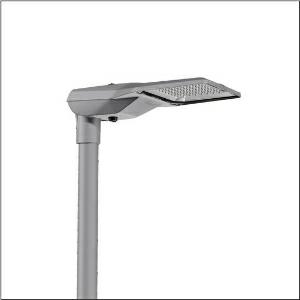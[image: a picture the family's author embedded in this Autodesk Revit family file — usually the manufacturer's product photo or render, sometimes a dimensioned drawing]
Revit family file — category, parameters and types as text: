
# Revit family: streetlight_sl_21_midi___st1_5a_5xe3p33t08lb_3dd1
name_source: partatom
category: Lighting Fixtures
units: mm (PartAtom-declared; Revit-internal decimal feet)

## family parameters
Cut with Voids When Loaded = No
Host = Face
Light Source = No
Part Type = Normal
Room Calculation Point = No
Round Connector Dimension = Use Diameter
Shared = No

## types (1)
- --- (1 x LED, 14100 lm, 99.6 W, 3000K)
    Apparent Load = 100 VA
    CIE Flux Codes = 22 53 95 100 100
    Color Rendering = 70
    Color Temperature = 3000K
    Default Elevation = 1800 mm
    Description = Streetlight SL 21 midi, mast luminaire, primary light control with lens, of PMMA, primary optical cover: cover, of toughened safety glass, transparent, light distribution: ST1.5a, light emission: direct distribution, primary light characteristic: asymmetric, installation type: side-entry, post-top, LED, High Power LED, rated luminous flux: 14.100lm, luminous efficacy: 142lm/W, light colour: 730, colour temperature: 3000K, control gear: D4i, control: overheat protection, constant luminous flux control, time-dependent luminous flux control, flexible luminous flux parameterisation, pre-setting: logarithmic dimming characteristic, mains connection: 230..240V, AC, 50/60Hz, start of lifetime: 100W, end of service life: 102W, reduction: 46W, luminaire housing, of diecast aluminium, powder-coated, SITECO metallic grey (DB 702S), corrosivity category C5 high according to DIN EN ISO 12944, please order mast flange separately, inclination adjustable: 0°, 5°, 10°, 15°, sealing non-destructively replaceable, multi-level sealing system, length: 644mm, width: 335mm, height: 110mm, mast flange for spigot size: 42mm (side-entry): 5XC10008XM4, 60/48mm (side-entry/post-top): 5XC10108XM2, 76/60mm (side-entry/post-top): 5XC10108XM1, mounting height: 4..8m, Smart Interface below and above, protection rating (complete): IP66, insulation class (complete): insulation class II (safety insulation), certification: CE, ENEC, ENEC+, VDE, impact resistance: IK10, permissible operating ambient temperature for outdoor applications: -40..+50°C, standard-compliant lighting for roads and squares, packaging unit: 1 piece

Light Distribution: ST1.5a
    Height = 111 mm
    Lamp = 1 x LED
    Lamp Light Flux = 14100 lm
    Lamp Power = 99.6 W
    Lamp count = 1
    Length = 644 mm
    Luminous efficacy = 142 lm/W
    Manufacturer = Siteco
    ModVariant = No
    Model = 5XE3P33T08LB
    Number of Poles = 1
    OnlyDefault = Yes
    Power Factor = 1
    Product Name = Streetlight SL 21 midi | ST1.5a
    Product group = mast luminaire | pylon top
    ProductGroupID = 6100
    Protection Class = Protection class II
    Protection Degree = IP 66
    RLX_Detail_Level = 1
    RLX_Emergency_Light_Flux = 0 lm
    RLX_Emergency_Type = 0
    RLX_Emergency_Type_DB = No
    RlxData = <blob elided: 30461 chars, md5=26ecb6d9>
    Socket = socket
    Standby Power = 0 W
    System Light Flux = 14100 lm
    System Power = 100 W
    Type Comments = factory setting: luminous flux: 100 % | dim-lin: 254 | 1020 mA
    Type Image = l_1004304.jpg
    URL = http://relux.com
    VarID = @adj_032491
    Voltage = 0 V
    Weight = 0.00 kg
    Width = 336 mm

## geometry (parser evidence)
native form markers: Blend x4, Sweep x11
no freeform markers — native parametric forms only
